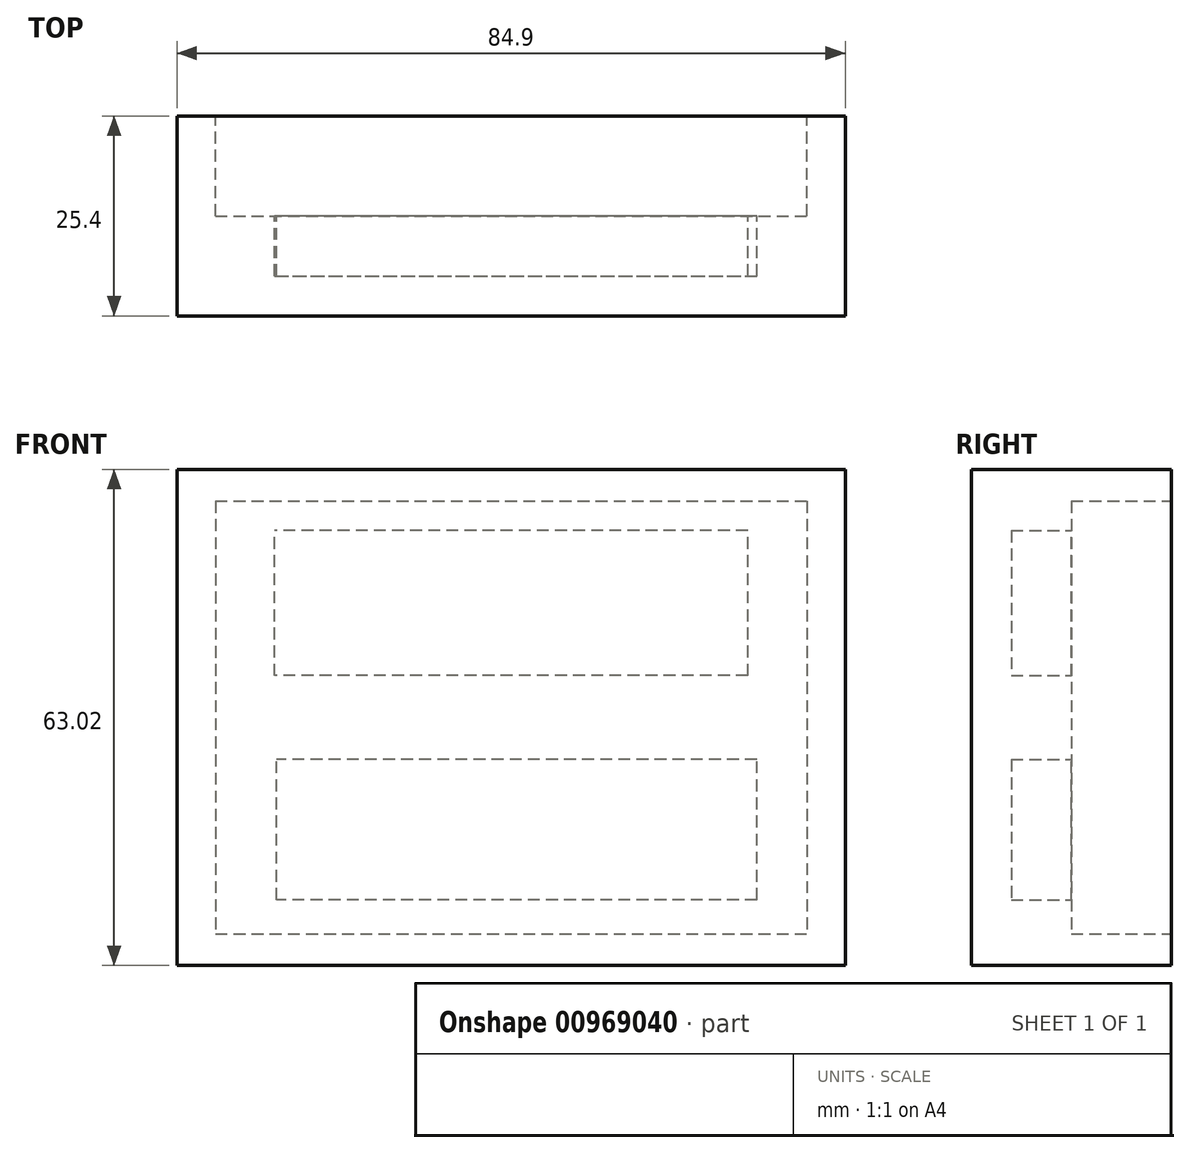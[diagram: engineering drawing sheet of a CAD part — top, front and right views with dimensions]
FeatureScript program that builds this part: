
annotation { "Feature Type Name" : "Feature", "Feature Type Description" : "" }
export const myFeature = defineFeature(function(context is Context, id is Id, definition is map)
    precondition{}
    {
        {
            var Q0;
            Q0=qCreatedBy(makeId("Front.planeOp"),FACE);
            var sketch = newSketch(context, id + "F0", { "sketchPlane" : qUnion([Q0])});
            skLineSegment(sketch, "E0.bottom", {"start": v(42.45, 31.51) * mm, "end": v(-42.45, 31.51) * mm});
            skLineSegment(sketch, "E0.top", {"start": v(42.45, -31.51) * mm, "end": v(-42.45, -31.51) * mm});
            skLineSegment(sketch, "E0.left", {"start": v(42.45, 31.51) * mm, "end": v(42.45, -31.51) * mm});
            skLineSegment(sketch, "E0.right", {"start": v(-42.45, 31.51) * mm, "end": v(-42.45, -31.51) * mm});
            skPoint(sketch, "E0.middle", {"position": v(0, 0) * mm});
            skLineSegment(sketch, "E1.bottom", {"start": v(-37.56, 27.49) * mm, "end": v(37.56, 27.49) * mm});
            skLineSegment(sketch, "E1.top", {"start": v(-37.56, -27.49) * mm, "end": v(37.56, -27.49) * mm});
            skLineSegment(sketch, "E1.left", {"start": v(-37.56, 27.49) * mm, "end": v(-37.56, -27.49) * mm});
            skLineSegment(sketch, "E1.right", {"start": v(37.56, 27.49) * mm, "end": v(37.56, -27.49) * mm});
            skLineSegment(sketch, "E2.bottom", {"start": v(-30.08, 23.74) * mm, "end": v(30.08, 23.74) * mm});
            skLineSegment(sketch, "E2.top", {"start": v(-30.08, 5.32) * mm, "end": v(30.08, 5.32) * mm});
            skLineSegment(sketch, "E2.left", {"start": v(-30.08, 23.74) * mm, "end": v(-30.08, 5.32) * mm});
            skLineSegment(sketch, "E2.right", {"start": v(30.08, 23.74) * mm, "end": v(30.08, 5.32) * mm});
            skLineSegment(sketch, "E3.bottom", {"start": v(-29.79, -5.32) * mm, "end": v(31.23, -5.32) * mm});
            skLineSegment(sketch, "E3.top", {"start": v(-29.79, -23.17) * mm, "end": v(31.23, -23.17) * mm});
            skLineSegment(sketch, "E3.left", {"start": v(-29.79, -5.32) * mm, "end": v(-29.79, -23.17) * mm});
            skLineSegment(sketch, "E3.right", {"start": v(31.23, -5.32) * mm, "end": v(31.23, -23.17) * mm});
            skSolve(sketch);
        }
        {
            var Q0;
            Q0=makeQuery(id+"F0.imprint","IMPRINT",FACE,{"disambiguationData":[TD([[makeQuery(id+"F0.imprint","IMPRINT",EDGE,{"derivedFrom":sQuery(id+"F0.wireOp",EDGE,"E0.bottom")}),1.0]])]});
            var Q1;
            Q1=makeQuery(id+"F0.imprint","IMPRINT",FACE,{"disambiguationData":[TD([[makeQuery(id+"F0.imprint","IMPRINT",EDGE,{"derivedFrom":sQuery(id+"F0.wireOp",EDGE,"E1.bottom")}),-1.0]])]});
            var Q2;
            Q2=makeQuery(id+"F0.imprint","IMPRINT",FACE,{"disambiguationData":[TD([[makeQuery(id+"F0.imprint","IMPRINT",EDGE,{"derivedFrom":sQuery(id+"F0.wireOp",EDGE,"E2.bottom")}),-1.0]])]});
            var Q3;
            Q3=makeQuery(id+"F0.imprint","IMPRINT",FACE,{"disambiguationData":[TD([[makeQuery(id+"F0.imprint","IMPRINT",EDGE,{"derivedFrom":sQuery(id+"F0.wireOp",EDGE,"E3.bottom")}),-1.0]])]});
            extrude(context, id + "F1", {"entities" : qUnion([Q0, Q1, Q2, Q3]), "depth" : 25.4 * mm, "offsetDistance" : 25.4 * mm});
        }
        {
            var Q0;
            Q0=makeQuery(id+"F0.imprint","IMPRINT",FACE,{"disambiguationData":[TD([[makeQuery(id+"F0.imprint","IMPRINT",EDGE,{"derivedFrom":sQuery(id+"F0.wireOp",EDGE,"E1.bottom")}),-1.0]])]});
            var Q1;
            Q1=makeQuery(id+"F0.imprint","IMPRINT",FACE,{"disambiguationData":[TD([[makeQuery(id+"F0.imprint","IMPRINT",EDGE,{"derivedFrom":sQuery(id+"F0.wireOp",EDGE,"E2.bottom")}),-1.0]])]});
            var Q2;
            Q2=makeQuery(id+"F0.imprint","IMPRINT",FACE,{"disambiguationData":[TD([[makeQuery(id+"F0.imprint","IMPRINT",EDGE,{"derivedFrom":sQuery(id+"F0.wireOp",EDGE,"E3.bottom")}),-1.0]])]});
            extrude(context, id + "F2", {"entities" : qUnion([Q0, Q1, Q2]), "operationType" : NewBodyOperationType.REMOVE, "depth" : 12.7 * mm, "offsetDistance" : 25.4 * mm});
        }
        {
            var Q0;
            Q0=makeQuery(id+"F0.imprint","IMPRINT",FACE,{"disambiguationData":[TD([[makeQuery(id+"F0.imprint","IMPRINT",EDGE,{"derivedFrom":sQuery(id+"F0.wireOp",EDGE,"E2.bottom")}),-1.0]])]});
            var Q1;
            Q1=makeQuery(id+"F0.imprint","IMPRINT",FACE,{"disambiguationData":[TD([[makeQuery(id+"F0.imprint","IMPRINT",EDGE,{"derivedFrom":sQuery(id+"F0.wireOp",EDGE,"E3.bottom")}),-1.0]])]});
            extrude(context, id + "F3", {"entities" : qUnion([Q0, Q1]), "operationType" : NewBodyOperationType.REMOVE, "depth" : 20.32 * mm, "offsetDistance" : 25.4 * mm});
        }
    });
